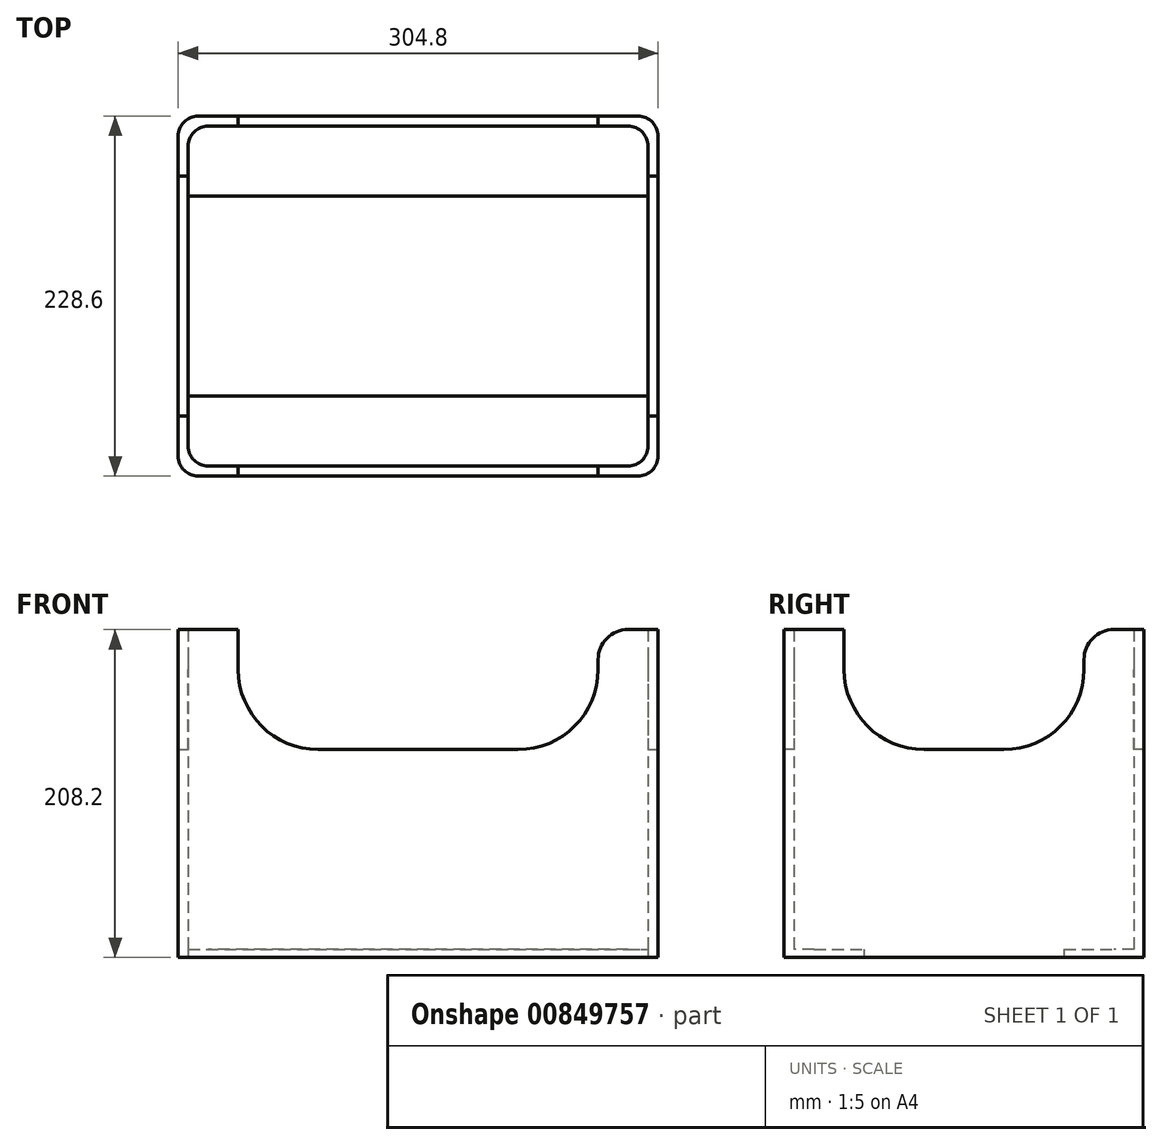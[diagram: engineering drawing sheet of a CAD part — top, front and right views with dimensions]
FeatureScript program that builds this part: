
annotation { "Feature Type Name" : "Feature", "Feature Type Description" : "" }
export const myFeature = defineFeature(function(context is Context, id is Id, definition is map)
    precondition{}
    {
        {
            var Q0;
            Q0=qCreatedBy(makeId("Top.planeOp"),FACE);
            var sketch = newSketch(context, id + "F0", { "sketchPlane" : qUnion([Q0])});
            skLineSegment(sketch, "E0.bottom", {"start": v(152.4, 114.3) * mm, "end": v(-152.4, 114.3) * mm});
            skLineSegment(sketch, "E0.top", {"start": v(152.4, -114.3) * mm, "end": v(-152.4, -114.3) * mm});
            skLineSegment(sketch, "E0.left", {"start": v(152.4, 114.3) * mm, "end": v(152.4, -114.3) * mm});
            skLineSegment(sketch, "E0.right", {"start": v(-152.4, 114.3) * mm, "end": v(-152.4, -114.3) * mm});
            skPoint(sketch, "E0.middle", {"position": v(0, 0) * mm});
            skLineSegment(sketch, "E1.bottom", {"start": v(-146.05, 63.5) * mm, "end": v(146.05, 63.5) * mm});
            skLineSegment(sketch, "E1.top", {"start": v(-146.05, -63.5) * mm, "end": v(146.05, -63.5) * mm});
            skLineSegment(sketch, "E1.left", {"start": v(-146.05, 63.5) * mm, "end": v(-146.05, -63.5) * mm});
            skLineSegment(sketch, "E1.right", {"start": v(146.05, 63.5) * mm, "end": v(146.05, -63.5) * mm});
            skSolve(sketch);
        }
        {
            var Q0;
            Q0=makeQuery(id+"F0.imprint","IMPRINT",FACE,{"disambiguationData":[TD([[makeQuery(id+"F0.imprint","IMPRINT",EDGE,{"derivedFrom":sQuery(id+"F0.wireOp",EDGE,"E0.bottom")}),1.0]])]});
            extrude(context, id + "F1", {"entities" : qUnion([Q0]), "depth" : 5 * mm, "offsetDistance" : 25 * mm});
        }
        {
            var Q0;
            Q0=makeQuery(id+"F1.opExtrude","CAP_FACE",FACE,{"disambiguationData":[OSD([sQuery(id+"F0.wireOp",EDGE,"E0.bottom"),sQuery(id+"F0.wireOp",EDGE,"E0.top"),sQuery(id+"F0.wireOp",EDGE,"E0.left"),sQuery(id+"F0.wireOp",EDGE,"E0.right"),sQuery(id+"F0.wireOp",EDGE,"E1.bottom"),sQuery(id+"F0.wireOp",EDGE,"E1.top"),sQuery(id+"F0.wireOp",EDGE,"E1.left"),sQuery(id+"F0.wireOp",EDGE,"E1.right")])],"isStart":false});
            var sketch = newSketch(context, id + "F2", { "sketchPlane" : qUnion([Q0])});
            skLineSegment(sketch, "E2.0", {"start": v(-146.05, 107.95) * mm, "end": v(-146.05, -107.95) * mm});
            skLineSegment(sketch, "E2.1", {"start": v(146.05, 107.95) * mm, "end": v(-146.05, 107.95) * mm});
            skLineSegment(sketch, "E2.2", {"start": v(146.05, 107.95) * mm, "end": v(146.05, -107.95) * mm});
            skLineSegment(sketch, "E2.3", {"start": v(146.05, -107.95) * mm, "end": v(-146.05, -107.95) * mm});
            skLineSegment(sketch, "E3.0", {"start": v(152.4, 114.3) * mm, "end": v(-152.4, 114.3) * mm});
            skLineSegment(sketch, "E3.1", {"start": v(-152.4, 114.3) * mm, "end": v(-152.4, -114.3) * mm});
            skLineSegment(sketch, "E3.2", {"start": v(152.4, 114.3) * mm, "end": v(152.4, -114.3) * mm});
            skLineSegment(sketch, "E3.3", {"start": v(152.4, -114.3) * mm, "end": v(-152.4, -114.3) * mm});
            skSolve(sketch);
        }
        {
            var Q0;
            {var subQ6=sQuery(id+"F2.wireOp",EDGE,"E2.1");Q0=makeQuery(id+"F2.imprint","IMPRINT",FACE,{"disambiguationData":[TD([[makeQuery(id+"F2.imprint","IMPRINT",EDGE,{"derivedFrom":subQ6}),-1.0]])]});}
            extrude(context, id + "F3", {"entities" : qUnion([Q0]), "operationType" : NewBodyOperationType.ADD, "depth" : 203.2 * mm, "offsetDistance" : 25.4 * mm});
        }
        {
            var Q0;
            Q0=makeQuery(id+"F3.boolean.opBoolean","MERGE",FACE,{"derivedFrom":[makeQuery(id+"F1.opExtrude","SWEPT_FACE",FACE,{"disambiguationData":[OSD([sQuery(id+"F0.wireOp",EDGE,"E0.top")])]}),makeQuery(id+"F3.opExtrude","SWEPT_FACE",FACE,{"disambiguationData":[OSD([sQuery(id+"F2.wireOp",EDGE,"E3.3")])]})]});
            var sketch = newSketch(context, id + "F4", { "sketchPlane" : qUnion([Q0])});
            skLineSegment(sketch, "E4.bottom", {"start": v(114.3, 208.2) * mm, "end": v(-114.3, 208.2) * mm});
            skLineSegment(sketch, "E4.top", {"start": v(114.3, 132) * mm, "end": v(-114.3, 132) * mm});
            skLineSegment(sketch, "E4.left", {"start": v(114.3, 208.2) * mm, "end": v(114.3, 132) * mm});
            skLineSegment(sketch, "E4.right", {"start": v(-114.3, 208.2) * mm, "end": v(-114.3, 132) * mm});
            skPoint(sketch, "E4.middle", {"position": v(0, 170.1) * mm});
            skSolve(sketch);
        }
        {
            var Q0;
            Q0 = qSketchRegion(id + "F4", true);
            extrude(context, id + "F5", {"entities" : qUnion([Q0]), "operationType" : NewBodyOperationType.REMOVE, "endBound" : BoundingType.THROUGH_ALL, "oppositeDirection" : true, "depth" : 25.4 * mm, "offsetDistance" : 25.4 * mm});
        }
        {
            var Q0;
            Q0=makeQuery(id+"F3.boolean.opBoolean","MERGE",FACE,{"derivedFrom":[makeQuery(id+"F1.opExtrude","SWEPT_FACE",FACE,{"disambiguationData":[OSD([sQuery(id+"F0.wireOp",EDGE,"E0.left")])]}),makeQuery(id+"F3.opExtrude","SWEPT_FACE",FACE,{"disambiguationData":[OSD([sQuery(id+"F2.wireOp",EDGE,"E3.2")])]})]});
            var sketch = newSketch(context, id + "F6", { "sketchPlane" : qUnion([Q0])});
            skLineSegment(sketch, "E5.bottom", {"start": v(76.2, 208.2) * mm, "end": v(-76.2, 208.2) * mm});
            skLineSegment(sketch, "E5.top", {"start": v(76.2, 132) * mm, "end": v(-76.2, 132) * mm});
            skLineSegment(sketch, "E5.left", {"start": v(76.2, 208.2) * mm, "end": v(76.2, 132) * mm});
            skLineSegment(sketch, "E5.right", {"start": v(-76.2, 208.2) * mm, "end": v(-76.2, 132) * mm});
            skPoint(sketch, "E5.middle", {"position": v(0, 170.1) * mm});
            skPoint(sketch, "E5.middle.positionSnap0", {"position": v(0, 208.2) * mm});
            skPoint(sketch, "E5.centerSnap0", {"position": v(0, 208.2) * mm});
            skSolve(sketch);
        }
        {
            var Q0;
            Q0 = qSketchRegion(id + "F6", true);
            extrude(context, id + "F7", {"entities" : qUnion([Q0]), "operationType" : NewBodyOperationType.REMOVE, "endBound" : BoundingType.THROUGH_ALL, "oppositeDirection" : true, "depth" : 25.4 * mm, "offsetDistance" : 25.4 * mm});
        }
        {
            var Q0;
            {var subQ0=sQuery(id+"F4.wireOp",EDGE,"E4.top");var subQ1=sQuery(id+"F4.wireOp",EDGE,"E4.right");Q0=makeQuery(id+"F5.boolean.opBoolean","COPY",EDGE,{"disambiguationData":[TD([makeQuery(id+"F1.opExtrude","SWEPT_FACE",FACE,{"disambiguationData":[OSD([sQuery(id+"F0.wireOp",EDGE,"E0.top")])]})])],"derivedFrom":makeQuery(id+"F5.opExtrude","SWEPT_EDGE",EDGE,{"disambiguationData":[OSD([subQ0,subQ1])]})});}
            var Q1;
            {var subQ0=sQuery(id+"F6.wireOp",EDGE,"E5.top");var subQ1=sQuery(id+"F6.wireOp",EDGE,"E5.left");Q1=makeQuery(id+"F7.boolean.opBoolean","COPY",EDGE,{"disambiguationData":[TD([makeQuery(id+"F1.opExtrude","SWEPT_FACE",FACE,{"disambiguationData":[OSD([sQuery(id+"F0.wireOp",EDGE,"E0.right")])]})])],"derivedFrom":makeQuery(id+"F7.opExtrude","SWEPT_EDGE",EDGE,{"disambiguationData":[OSD([subQ0,subQ1])]})});}
            var Q2;
            {var subQ0=sQuery(id+"F4.wireOp",EDGE,"E4.top");var subQ1=sQuery(id+"F4.wireOp",EDGE,"E4.right");Q2=makeQuery(id+"F5.boolean.opBoolean","COPY",EDGE,{"disambiguationData":[TD([makeQuery(id+"F1.opExtrude","SWEPT_FACE",FACE,{"disambiguationData":[OSD([sQuery(id+"F0.wireOp",EDGE,"E0.bottom")])]})])],"derivedFrom":makeQuery(id+"F5.opExtrude","SWEPT_EDGE",EDGE,{"disambiguationData":[OSD([subQ0,subQ1])]})});}
            var Q3;
            {var subQ0=sQuery(id+"F6.wireOp",EDGE,"E5.right");var subQ1=sQuery(id+"F6.wireOp",EDGE,"E5.top");Q3=makeQuery(id+"F7.boolean.opBoolean","COPY",EDGE,{"disambiguationData":[TD([makeQuery(id+"F1.opExtrude","SWEPT_FACE",FACE,{"disambiguationData":[OSD([sQuery(id+"F0.wireOp",EDGE,"E0.right")])]})])],"derivedFrom":makeQuery(id+"F7.opExtrude","SWEPT_EDGE",EDGE,{"disambiguationData":[OSD([subQ1,subQ0])]})});}
            var Q4;
            {var subQ0=sQuery(id+"F4.wireOp",EDGE,"E4.top");var subQ1=sQuery(id+"F4.wireOp",EDGE,"E4.left");Q4=makeQuery(id+"F5.boolean.opBoolean","COPY",EDGE,{"disambiguationData":[TD([makeQuery(id+"F1.opExtrude","SWEPT_FACE",FACE,{"disambiguationData":[OSD([sQuery(id+"F0.wireOp",EDGE,"E0.bottom")])]})])],"derivedFrom":makeQuery(id+"F5.opExtrude","SWEPT_EDGE",EDGE,{"disambiguationData":[OSD([subQ0,subQ1])]})});}
            var Q5;
            {var subQ0=sQuery(id+"F6.wireOp",EDGE,"E5.right");var subQ1=sQuery(id+"F6.wireOp",EDGE,"E5.top");Q5=makeQuery(id+"F7.boolean.opBoolean","COPY",EDGE,{"disambiguationData":[TD([makeQuery(id+"F1.opExtrude","SWEPT_FACE",FACE,{"disambiguationData":[OSD([sQuery(id+"F0.wireOp",EDGE,"E0.left")])]})])],"derivedFrom":makeQuery(id+"F7.opExtrude","SWEPT_EDGE",EDGE,{"disambiguationData":[OSD([subQ1,subQ0])]})});}
            var Q6;
            {var subQ0=sQuery(id+"F4.wireOp",EDGE,"E4.top");var subQ1=sQuery(id+"F4.wireOp",EDGE,"E4.left");Q6=makeQuery(id+"F5.boolean.opBoolean","COPY",EDGE,{"disambiguationData":[TD([makeQuery(id+"F1.opExtrude","SWEPT_FACE",FACE,{"disambiguationData":[OSD([sQuery(id+"F0.wireOp",EDGE,"E0.top")])]})])],"derivedFrom":makeQuery(id+"F5.opExtrude","SWEPT_EDGE",EDGE,{"disambiguationData":[OSD([subQ0,subQ1])]})});}
            var Q7;
            {var subQ0=sQuery(id+"F6.wireOp",EDGE,"E5.left");var subQ1=sQuery(id+"F6.wireOp",EDGE,"E5.top");Q7=makeQuery(id+"F7.boolean.opBoolean","COPY",EDGE,{"disambiguationData":[TD([makeQuery(id+"F1.opExtrude","SWEPT_FACE",FACE,{"disambiguationData":[OSD([sQuery(id+"F0.wireOp",EDGE,"E0.left")])]})])],"derivedFrom":makeQuery(id+"F7.opExtrude","SWEPT_EDGE",EDGE,{"disambiguationData":[OSD([subQ1,subQ0])]})});}
            fillet(context, id + "F8", {"entities" : qUnion([Q0, Q1, Q2, Q3, Q4, Q5, Q6, Q7]), "radius" : 50.8 * mm, "tangentPropagation" : true, "allowEdgeOverflow" : false});
        }
        {
            var Q0;
            {var subQ1=sQuery(id+"F2.wireOp",EDGE,"E3.2");var subQ2=sQuery(id+"F6.wireOp",EDGE,"E5.left");Q0=makeQuery(id+"F7.boolean.opBoolean","COPY",EDGE,{"disambiguationData":[TD([makeQuery(id+"F1.opExtrude","SWEPT_FACE",FACE,{"disambiguationData":[OSD([sQuery(id+"F0.wireOp",EDGE,"E0.left")])]})])],"derivedFrom":makeQuery(id+"F7.opExtrude","SWEPT_EDGE",EDGE,{"disambiguationData":[OSD([subQ1,sQuery(id+"F6.wireOp",EDGE,"E5.bottom"),subQ2])]})});}
            var Q1;
            {var subQ2=sQuery(id+"F2.wireOp",EDGE,"E3.3");var subQ3=sQuery(id+"F4.wireOp",EDGE,"E4.left");Q1=makeQuery(id+"F5.boolean.opBoolean","COPY",EDGE,{"disambiguationData":[TD([makeQuery(id+"F1.opExtrude","SWEPT_FACE",FACE,{"disambiguationData":[OSD([sQuery(id+"F0.wireOp",EDGE,"E0.bottom")])]})])],"derivedFrom":makeQuery(id+"F5.opExtrude","SWEPT_EDGE",EDGE,{"disambiguationData":[OSD([subQ2,sQuery(id+"F4.wireOp",EDGE,"E4.bottom"),subQ3])]})});}
            var Q2;
            {var subQ2=sQuery(id+"F2.wireOp",EDGE,"E3.3");var subQ3=sQuery(id+"F4.wireOp",EDGE,"E4.right");Q2=makeQuery(id+"F5.boolean.opBoolean","COPY",EDGE,{"disambiguationData":[TD([makeQuery(id+"F1.opExtrude","SWEPT_FACE",FACE,{"disambiguationData":[OSD([sQuery(id+"F0.wireOp",EDGE,"E0.bottom")])]})])],"derivedFrom":makeQuery(id+"F5.opExtrude","SWEPT_EDGE",EDGE,{"disambiguationData":[OSD([subQ2,sQuery(id+"F4.wireOp",EDGE,"E4.bottom"),subQ3])]})});}
            var Q3;
            {var subQ2=sQuery(id+"F2.wireOp",EDGE,"E3.2");var subQ3=sQuery(id+"F6.wireOp",EDGE,"E5.left");Q3=makeQuery(id+"F7.boolean.opBoolean","COPY",EDGE,{"disambiguationData":[TD([makeQuery(id+"F1.opExtrude","SWEPT_FACE",FACE,{"disambiguationData":[OSD([sQuery(id+"F0.wireOp",EDGE,"E0.right")])]})])],"derivedFrom":makeQuery(id+"F7.opExtrude","SWEPT_EDGE",EDGE,{"disambiguationData":[OSD([subQ2,sQuery(id+"F6.wireOp",EDGE,"E5.bottom"),subQ3])]})});}
            var Q4;
            {var subQ2=sQuery(id+"F2.wireOp",EDGE,"E3.2");var subQ3=sQuery(id+"F6.wireOp",EDGE,"E5.right");Q4=makeQuery(id+"F7.boolean.opBoolean","COPY",EDGE,{"disambiguationData":[TD([makeQuery(id+"F1.opExtrude","SWEPT_FACE",FACE,{"disambiguationData":[OSD([sQuery(id+"F0.wireOp",EDGE,"E0.right")])]})])],"derivedFrom":makeQuery(id+"F7.opExtrude","SWEPT_EDGE",EDGE,{"disambiguationData":[OSD([subQ2,sQuery(id+"F6.wireOp",EDGE,"E5.bottom"),subQ3])]})});}
            var Q5;
            {var subQ0=sQuery(id+"F2.wireOp",EDGE,"E3.3");var subQ2=sQuery(id+"F4.wireOp",EDGE,"E4.right");Q5=makeQuery(id+"F5.boolean.opBoolean","COPY",EDGE,{"disambiguationData":[TD([makeQuery(id+"F1.opExtrude","SWEPT_FACE",FACE,{"disambiguationData":[OSD([sQuery(id+"F0.wireOp",EDGE,"E0.top")])]})])],"derivedFrom":makeQuery(id+"F5.opExtrude","SWEPT_EDGE",EDGE,{"disambiguationData":[OSD([subQ0,sQuery(id+"F4.wireOp",EDGE,"E4.bottom"),subQ2])]})});}
            var Q6;
            {var subQ0=sQuery(id+"F2.wireOp",EDGE,"E3.3");var subQ1=sQuery(id+"F4.wireOp",EDGE,"E4.left");Q6=makeQuery(id+"F5.boolean.opBoolean","COPY",EDGE,{"disambiguationData":[TD([makeQuery(id+"F1.opExtrude","SWEPT_FACE",FACE,{"disambiguationData":[OSD([sQuery(id+"F0.wireOp",EDGE,"E0.top")])]})])],"derivedFrom":makeQuery(id+"F5.opExtrude","SWEPT_EDGE",EDGE,{"disambiguationData":[OSD([subQ0,sQuery(id+"F4.wireOp",EDGE,"E4.bottom"),subQ1])]})});}
            var Q7;
            {var subQ1=sQuery(id+"F6.wireOp",EDGE,"E5.right");var subQ2=sQuery(id+"F2.wireOp",EDGE,"E3.2");Q7=makeQuery(id+"F7.boolean.opBoolean","COPY",EDGE,{"disambiguationData":[TD([makeQuery(id+"F1.opExtrude","SWEPT_FACE",FACE,{"disambiguationData":[OSD([sQuery(id+"F0.wireOp",EDGE,"E0.left")])]})])],"derivedFrom":makeQuery(id+"F7.opExtrude","SWEPT_EDGE",EDGE,{"disambiguationData":[OSD([subQ2,sQuery(id+"F6.wireOp",EDGE,"E5.bottom"),subQ1])]})});}
            fillet(context, id + "F9", {"entities" : qUnion([Q0, Q1, Q2, Q3, Q4, Q5, Q6, Q7]), "radius" : 19.05 * mm, "tangentPropagation" : true, "allowEdgeOverflow" : false});
        }
        {
            var Q0;
            Q0=makeQuery(id+"F3.boolean.opBoolean","MERGE",EDGE,{"derivedFrom":[makeQuery(id+"F1.opExtrude","SWEPT_EDGE",EDGE,{"disambiguationData":[OSD([sQuery(id+"F0.wireOp",EDGE,"E0.top"),sQuery(id+"F0.wireOp",EDGE,"E0.left")])]}),makeQuery(id+"F3.opExtrude","SWEPT_EDGE",EDGE,{"disambiguationData":[OSD([sQuery(id+"F2.wireOp",EDGE,"E3.2"),sQuery(id+"F2.wireOp",EDGE,"E3.3")])]})]});
            var Q1;
            Q1=makeQuery(id+"F3.opExtrude","SWEPT_EDGE",EDGE,{"disambiguationData":[OSD([sQuery(id+"F2.wireOp",EDGE,"E2.2"),sQuery(id+"F2.wireOp",EDGE,"E2.3")])]});
            var Q2;
            Q2=makeQuery(id+"F3.boolean.opBoolean","MERGE",EDGE,{"derivedFrom":[makeQuery(id+"F1.opExtrude","SWEPT_EDGE",EDGE,{"disambiguationData":[OSD([sQuery(id+"F0.wireOp",EDGE,"E0.top"),sQuery(id+"F0.wireOp",EDGE,"E0.right")])]}),makeQuery(id+"F3.opExtrude","SWEPT_EDGE",EDGE,{"disambiguationData":[OSD([sQuery(id+"F2.wireOp",EDGE,"E3.1"),sQuery(id+"F2.wireOp",EDGE,"E3.3")])]})]});
            var Q3;
            Q3=makeQuery(id+"F3.opExtrude","SWEPT_EDGE",EDGE,{"disambiguationData":[OSD([sQuery(id+"F2.wireOp",EDGE,"E2.1"),sQuery(id+"F2.wireOp",EDGE,"E2.2")])]});
            var Q4;
            Q4=makeQuery(id+"F3.opExtrude","SWEPT_EDGE",EDGE,{"disambiguationData":[OSD([sQuery(id+"F2.wireOp",EDGE,"E2.0"),sQuery(id+"F2.wireOp",EDGE,"E2.1")])]});
            var Q5;
            Q5=makeQuery(id+"F3.opExtrude","SWEPT_EDGE",EDGE,{"disambiguationData":[OSD([sQuery(id+"F2.wireOp",EDGE,"E2.0"),sQuery(id+"F2.wireOp",EDGE,"E2.3")])]});
            var Q6;
            Q6=makeQuery(id+"F3.boolean.opBoolean","MERGE",EDGE,{"derivedFrom":[makeQuery(id+"F1.opExtrude","SWEPT_EDGE",EDGE,{"disambiguationData":[OSD([sQuery(id+"F0.wireOp",EDGE,"E0.bottom"),sQuery(id+"F0.wireOp",EDGE,"E0.right")])]}),makeQuery(id+"F3.opExtrude","SWEPT_EDGE",EDGE,{"disambiguationData":[OSD([sQuery(id+"F2.wireOp",EDGE,"E3.0"),sQuery(id+"F2.wireOp",EDGE,"E3.1")])]})]});
            var Q7;
            Q7=makeQuery(id+"F3.boolean.opBoolean","MERGE",EDGE,{"derivedFrom":[makeQuery(id+"F1.opExtrude","SWEPT_EDGE",EDGE,{"disambiguationData":[OSD([sQuery(id+"F0.wireOp",EDGE,"E0.bottom"),sQuery(id+"F0.wireOp",EDGE,"E0.left")])]}),makeQuery(id+"F3.opExtrude","SWEPT_EDGE",EDGE,{"disambiguationData":[OSD([sQuery(id+"F2.wireOp",EDGE,"E3.0"),sQuery(id+"F2.wireOp",EDGE,"E3.2")])]})]});
            fillet(context, id + "F10", {"entities" : qUnion([Q0, Q1, Q2, Q3, Q4, Q5, Q6, Q7]), "radius" : 12.7 * mm, "tangentPropagation" : true, "allowEdgeOverflow" : false});
        }
    });
